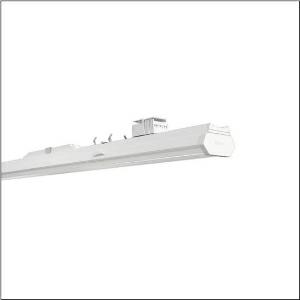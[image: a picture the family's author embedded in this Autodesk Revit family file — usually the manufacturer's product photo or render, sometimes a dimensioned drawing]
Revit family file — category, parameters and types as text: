
# Revit family: licross_r__11_protected_mo_51tp11dn495g_6ace
name_source: partatom
category: Lighting Fixtures
units: mm (PartAtom-declared; Revit-internal decimal feet)

## family parameters
Cut with Voids When Loaded = No
Host = Face
Light Source = No
Part Type = Normal
Room Calculation Point = No
Round Connector Dimension = Use Diameter
Shared = No

## types (1)
- --- (1 x LED, 9930 lm, 57.1 W, 4000K)
    Apparent Load = 57 VA
    CIE Flux Codes = 83 94 98 100 100
    Color Rendering = 80
    Color Temperature = 4000K
    Default Elevation = 1800 mm
    Description = Licross® 11 Protected MO, luminaire insert, of sheet steel, galvanised, coil coated, white, length: 1.500mm, width: 90mm, height: 101mm, LED rated luminous flux: 9.980lm, light colour: 840, control gear: DALI 2, control gear: ECG DALI, with plug, 5-pole, with phase selection, mains connection: 220..240V, AC, 50/60Hz, halogen-free wiring, primary light control with lens, of plastic, primary optical cover: cover, of PMMA, light emission: direct with ceiling illumination distribution, primary light characteristic: symmetric, protection rating (complete): IP64, insulation class (complete): insulation class I (protective earthing), certification: CE, ENEC, VDE, UKCA, protection symbol: D if used in an environment with conductive dust loads with corresponding accessories, impact resistance: IK06, permissible ambient temperature for indoor applications: -25..+35°C, corresponds to IFS (International Featured Standards) requirements for safety and quality in the food industry, reducing of maximum allowable ambient temperature of 5°C with ceiling mounting, LABS conformity tested according to VDMA 24364:2018-05, packaging unit: 1 piece
    Height = 92 mm
    Lamp = 1 x LED
    Lamp Light Flux = 9930 lm
    Lamp Power = 57.1 W
    Lamp count = 1
    Length = 1500 mm
    Luminous efficacy = 174 lm/W
    Manufacturer = Siteco
    ModVariant = No
    Model = 51TP11DN495G
    Mounting Place = Ceiling
    Mounting Type = Pendant
    Number of Poles = 1
    OnlyDefault = Yes
    Power Factor = 1
    Product Name = Licross® 11 Protected MO
    Product group = luminaire insert
    ProductGroupID = 902
    Protection Class = Protection class I
    Protection Degree = IP 64
    RLX_Detail_Level = 1
    RlxData = <blob elided: 24133 chars, md5=9b2149cf>
    Socket = socket
    Standby Power = 0 W
    System Light Flux = 9930 lm
    System Power = 57 W
    Type Comments = factory setting: luminous flux: 100 % | dim-lin: 254 | 378 mA
    Type Image = l_1256148.jpg
    URL = http://relux.com
    VarID = @adj_010081
    Voltage = 0 V
    Weight = 0.00 kg
    Width = 88 mm

## geometry (parser evidence)
native form markers: Blend x4, Sweep x13
no freeform markers — native parametric forms only
